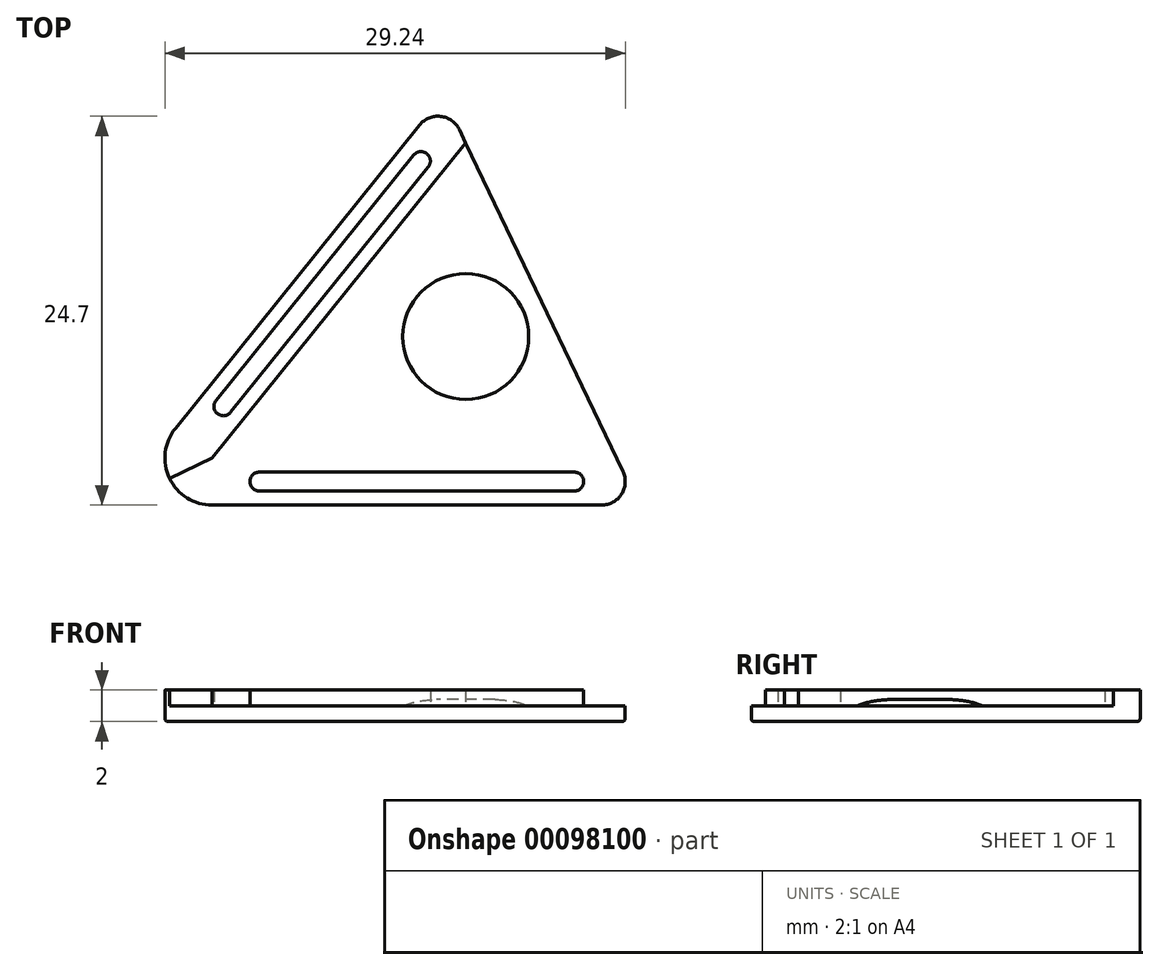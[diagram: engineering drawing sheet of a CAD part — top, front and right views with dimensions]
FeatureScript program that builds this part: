
annotation { "Feature Type Name" : "Feature", "Feature Type Description" : "" }
export const myFeature = defineFeature(function(context is Context, id is Id, definition is map)
    precondition{}
    {
        {
            var Q0;
            Q0=qCreatedBy(makeId("Top.planeOp"),FACE);
            var sketch = newSketch(context, id + "F0", { "sketchPlane" : qUnion([Q0])});
            skLineSegment(sketch, "E0", {"start": v(-16.1, 0) * mm, "end": v(0, 20) * mm});
            skLineSegment(sketch, "E1", {"start": v(0, 20) * mm, "end": v(9.57, 0) * mm});
            skLineSegment(sketch, "E2", {"start": v(9.57, 0) * mm, "end": v(-16.1, 0) * mm});
            skSolve(sketch);
        }
        {
            var Q0;
            Q0=makeQuery(id+"F0.imprint","IMPRINT",FACE,{"disambiguationData":[TD([[makeQuery(id+"F0.imprint","IMPRINT",EDGE,{"derivedFrom":sQuery(id+"F0.wireOp",EDGE,"E0")}),-1.0]])]});
            var sketch = newSketch(context, id + "F1", { "sketchPlane" : qUnion([Q0])});
            skLineSegment(sketch, "E3", {"start": v(-18.45, 1.88) * mm, "end": v(-1.44, 23) * mm});
            skLineSegment(sketch, "E4", {"start": v(-1.44, 23) * mm, "end": v(11, -3) * mm});
            skLineSegment(sketch, "E5", {"start": v(11, -3) * mm, "end": v(-16.1, -3) * mm});
            skPoint(sketch, "E6.visualSharp", {"position": v(-22.38, -3) * mm});
            skArc(sketch, "E6.filletArc", {"start": v(-18.45, 1.88) * mm, "mid": v(-18.82, -1.3) * mm, "end": v(-16.1, -3) * mm});
            skSolve(sketch);
        }
        {
            var Q0;
            Q0=makeQuery(id+"F0.imprint","IMPRINT",FACE,{"disambiguationData":[TD([[makeQuery(id+"F0.imprint","IMPRINT",EDGE,{"derivedFrom":sQuery(id+"F0.wireOp",EDGE,"E0")}),-1.0]])]});
            var Q1;
            {var subQ4=sQuery(id+"F1.wireOp",EDGE,"E3");Q1=makeQuery(id+"F1.imprint","IMPRINT",FACE,{"disambiguationData":[TD([[makeQuery(id+"F1.imprint","IMPRINT",EDGE,{"derivedFrom":subQ4}),-1.0]])]});}
            extrude(context, id + "F2", {"entities" : qUnion([Q0, Q1]), "depth" : 1 * mm});
        }
        {
            var Q0;
            Q0=makeQuery(id+"F2.opExtrude","CAP_FACE",FACE,{"disambiguationData":[OSD([sQuery(id+"F0.wireOp",EDGE,"E0"),sQuery(id+"F0.wireOp",EDGE,"E2"),sQuery(id+"F1.wireOp",EDGE,"E3"),sQuery(id+"F1.wireOp",EDGE,"E4"),sQuery(id+"F1.wireOp",EDGE,"E5")])],"isStart":false});
            var sketch = newSketch(context, id + "F3", { "sketchPlane" : qUnion([Q0])});
            skLineSegment(sketch, "E7", {"start": v(-16.1, 0) * mm, "end": v(0, 20) * mm});
            skLineSegment(sketch, "E8", {"start": v(0, 20) * mm, "end": v(-1.44, 23) * mm});
            skLineSegment(sketch, "E9", {"start": v(-1.44, 23) * mm, "end": v(-18.45, 1.88) * mm});
            skLineSegment(sketch, "E10", {"start": v(-16.1, 0) * mm, "end": v(-18.45, 1.88) * mm, "construction": true});
            skLineSegment(sketch, "E11", {"start": v(-13.1, -0.9) * mm, "end": v(6.9, -0.9) * mm});
            skLineSegment(sketch, "E12", {"start": v(6.9, -0.9) * mm, "end": v(6.9, -2.1) * mm, "construction": true});
            skLineSegment(sketch, "E13", {"start": v(6.9, -2.1) * mm, "end": v(-13.1, -2.1) * mm});
            skLineSegment(sketch, "E14", {"start": v(-13.1, -2.1) * mm, "end": v(-13.1, -0.9) * mm, "construction": true});
            skArc(sketch, "E15", {"start": v(6.9, -2.1) * mm, "mid": v(7.5, -1.5) * mm, "end": v(6.9, -0.9) * mm});
            skArc(sketch, "E16", {"start": v(-13.1, -0.9) * mm, "mid": v(-13.7, -1.5) * mm, "end": v(-13.1, -2.1) * mm});
            skLineSegment(sketch, "E17", {"start": v(-16.1, 0) * mm, "end": v(-16.1, -3) * mm, "construction": true});
            skLineSegment(sketch, "E18", {"start": v(-16.1, -1.5) * mm, "end": v(-4.74, -1.5) * mm, "construction": true});
            skLineSegment(sketch, "E19", {"start": v(-17.28, 0.94) * mm, "end": v(-10.44, 9.43) * mm, "construction": true});
            skLineSegment(sketch, "E20", {"start": v(-15.86, 3.65) * mm, "end": v(-3.32, 19.23) * mm});
            skLineSegment(sketch, "E21", {"start": v(-3.32, 19.23) * mm, "end": v(-2.38, 18.48) * mm, "construction": true});
            skLineSegment(sketch, "E22", {"start": v(-2.38, 18.48) * mm, "end": v(-14.93, 2.9) * mm});
            skLineSegment(sketch, "E23", {"start": v(-14.93, 2.9) * mm, "end": v(-15.86, 3.65) * mm, "construction": true});
            skPoint(sketch, "E24", {"position": v(-15.4, 3.28) * mm});
            skArc(sketch, "E25", {"start": v(-15.86, 3.65) * mm, "mid": v(-15.77, 2.81) * mm, "end": v(-14.93, 2.9) * mm});
            skArc(sketch, "E26", {"start": v(-2.38, 18.48) * mm, "mid": v(-2.47, 19.32) * mm, "end": v(-3.32, 19.23) * mm});
            skLineSegment(sketch, "E27", {"start": v(-16.1, 0) * mm, "end": v(-18.82, -1.3) * mm});
            skLineSegment(sketch, "E28", {"start": v(-18.45, 1.88) * mm, "end": v(-18.45, 1.88) * mm});
            skLineSegment(sketch, "E29", {"start": v(-18.82, -1.3) * mm, "end": v(-18.82, -1.3) * mm});
            skPoint(sketch, "E30.visualSharp", {"position": v(-19.63, 0.4) * mm});
            skArc(sketch, "E30.filletArc", {"start": v(-18.45, 1.88) * mm, "mid": v(-19.09, 0.35) * mm, "end": v(-18.82, -1.3) * mm});
            skSolve(sketch);
        }
        {
            var Q0;
            Q0=makeQuery(id+"F3.imprint","IMPRINT",FACE,{"disambiguationData":[TD([[makeQuery(id+"F3.imprint","IMPRINT",EDGE,{"derivedFrom":sQuery(id+"F3.wireOp",EDGE,"E7")}),1.0]])]});
            var Q1;
            Q1=makeQuery(id+"F3.imprint","IMPRINT",FACE,{"disambiguationData":[TD([[makeQuery(id+"F3.imprint","IMPRINT",EDGE,{"derivedFrom":sQuery(id+"F3.wireOp",EDGE,"E11")}),-1.0]])]});
            extrude(context, id + "F4", {"entities" : qUnion([Q0, Q1]), "depth" : 1 * mm});
        }
        {
            var Q0;
            Q0=makeQuery(id+"F4.opExtrude","SWEPT_EDGE",EDGE,{"disambiguationData":[OSD([sQuery(id+"F3.wireOp",EDGE,"E8"),sQuery(id+"F3.wireOp",EDGE,"E9")])]});
            var Q1;
            Q1=makeQuery(id+"F2.opExtrude","SWEPT_EDGE",EDGE,{"disambiguationData":[OSD([sQuery(id+"F1.wireOp",EDGE,"E3"),sQuery(id+"F1.wireOp",EDGE,"E4")])]});
            var Q2;
            Q2=makeQuery(id+"F2.opExtrude","SWEPT_EDGE",EDGE,{"disambiguationData":[OSD([sQuery(id+"F1.wireOp",EDGE,"E4"),sQuery(id+"F1.wireOp",EDGE,"E5")])]});
            fillet(context, id + "F5", {"entities" : qUnion([Q0, Q1, Q2]), "radius" : 1.5 * mm, "tangentPropagation" : true, "allowEdgeOverflow" : false});
        }
        {
            var Q0;
            Q0=makeQuery(id+"F2.opExtrude","CAP_FACE",FACE,{"disambiguationData":[OSD([sQuery(id+"F0.wireOp",EDGE,"E0"),sQuery(id+"F0.wireOp",EDGE,"E1"),sQuery(id+"F0.wireOp",EDGE,"E2")])],"isStart":false});
            var sketch = newSketch(context, id + "F6", { "sketchPlane" : qUnion([Q0])});
            skLineSegment(sketch, "E31", {"start": v(-16.1, 0) * mm, "end": v(4.79, 10) * mm, "construction": true});
            skCircle(sketch, "E32", {"center": v(0, 7.7) * mm, "radius": 4 * mm});
            skSolve(sketch);
        }
        {
            var Q0;
            Q0=makeQuery(id+"F6.imprint","IMPRINT",FACE,{"disambiguationData":[TD([[makeQuery(id+"F6.imprint","IMPRINT",EDGE,{"derivedFrom":sQuery(id+"F6.wireOp",EDGE,"E32")}),1.0]])]});
            extrude(context, id + "F7", {"entities" : qUnion([Q0]), "operationType" : NewBodyOperationType.ADD, "depth" : 0.4 * mm});
        }
        {
            var Q0;
            Q0=makeQuery(id+"F7.opExtrude","CAP_EDGE",EDGE,{"disambiguationData":[OSD([sQuery(id+"F6.wireOp",EDGE,"E32")])],"isStart":false});
            fillet(context, id + "F8", {"entities" : qUnion([Q0]), "radius" : 6 * mm, "tangentPropagation" : true, "allowEdgeOverflow" : false});
        }
        {
            var Q0;
            Q0=makeQuery(id+"F4.opExtrude","SWEPT_BODY",BODY,{"disambiguationData":[OSD([sQuery(id+"F3.wireOp",EDGE,"E7"),sQuery(id+"F3.wireOp",EDGE,"E8"),sQuery(id+"F3.wireOp",EDGE,"E9"),sQuery(id+"F3.wireOp",EDGE,"E20"),sQuery(id+"F3.wireOp",EDGE,"E22"),sQuery(id+"F3.wireOp",EDGE,"E25"),sQuery(id+"F3.wireOp",EDGE,"E26"),sQuery(id+"F3.wireOp",EDGE,"E27"),sQuery(id+"F3.wireOp",EDGE,"E30.filletArc")])]});
            var Q1;
            Q1=makeQuery(id+"F2.opExtrude","SWEPT_BODY",BODY,{"disambiguationData":[OSD([sQuery(id+"F0.wireOp",EDGE,"E0"),sQuery(id+"F0.wireOp",EDGE,"E1"),sQuery(id+"F0.wireOp",EDGE,"E2")])]});
            var Q2;
            Q2=makeQuery(id+"F2.opExtrude","SWEPT_BODY",BODY,{"disambiguationData":[OSD([sQuery(id+"F0.wireOp",EDGE,"E0"),sQuery(id+"F0.wireOp",EDGE,"E2"),sQuery(id+"F1.wireOp",EDGE,"E3"),sQuery(id+"F1.wireOp",EDGE,"E4"),sQuery(id+"F1.wireOp",EDGE,"E5"),sQuery(id+"F1.wireOp",EDGE,"E6.filletArc")])]});
            booleanBodies(context, id + "F9", {"operationType" : BooleanOperationType.UNION, "tools" : qUnion([Q0, Q1, Q2])});
        }
        {
            var Q0;
            {var subQ0=sQuery(id+"F1.wireOp",EDGE,"E4");Q0=makeQuery(id+"F9.opBoolean","MERGE",EDGE,{"derivedFrom":[makeQuery(id+"F2.opExtrude","CAP_EDGE",EDGE,{"disambiguationData":[OSD([sQuery(id+"F0.wireOp",EDGE,"E1")])],"isStart":true}),makeQuery(id+"F2.opExtrude","CAP_EDGE",EDGE,{"disambiguationData":[OSD([subQ0]),TDD([makeQuery(id+"F1.imprint","IMPRINT",EDGE,{"disambiguationData":[TD([[makeQuery(id+"F1.imprint","INTERSECT",VERTEX,{"derivedFrom":[makeQuery(id+"F0.imprint","IMPRINT",EDGE,{"derivedFrom":sQuery(id+"F0.wireOp",EDGE,"E0")}),subQ0]}),1.0]])],"derivedFrom":subQ0})])],"isStart":true}),makeQuery(id+"F2.opExtrude","CAP_EDGE",EDGE,{"disambiguationData":[OSD([subQ0]),TDD([makeQuery(id+"F1.imprint","IMPRINT",EDGE,{"disambiguationData":[TD([[makeQuery(id+"F1.imprint","INTERSECT",VERTEX,{"derivedFrom":[makeQuery(id+"F0.imprint","IMPRINT",EDGE,{"derivedFrom":sQuery(id+"F0.wireOp",EDGE,"E2")}),subQ0]}),-1.0]])],"derivedFrom":subQ0})])],"isStart":true})]});}
            var Q1;
            {var subQ0=sQuery(id+"F1.wireOp",EDGE,"E4");var subQ1=sQuery(id+"F1.wireOp",EDGE,"E3");Q1=makeQuery(id+"F5.opFillet","BLEND_EDGE",EDGE,{"blendedFrom":[makeQuery(id+"F2.opExtrude","SWEPT_EDGE",EDGE,{"disambiguationData":[OSD([subQ1,subQ0])]}),makeQuery(id+"F2.opExtrude","CAP_FACE",FACE,{"disambiguationData":[OSD([sQuery(id+"F0.wireOp",EDGE,"E0"),sQuery(id+"F0.wireOp",EDGE,"E2"),subQ1,subQ0,sQuery(id+"F1.wireOp",EDGE,"E5"),sQuery(id+"F1.wireOp",EDGE,"E6.filletArc")])],"isStart":true})],"blendedInto":[makeQuery(id+"F2.opExtrude","CAP_FACE",FACE,{"disambiguationData":[OSD([sQuery(id+"F0.wireOp",EDGE,"E0"),sQuery(id+"F0.wireOp",EDGE,"E2"),subQ1,subQ0,sQuery(id+"F1.wireOp",EDGE,"E5"),sQuery(id+"F1.wireOp",EDGE,"E6.filletArc")])],"isStart":true})]});}
            var Q2;
            Q2=makeQuery(id+"F2.opExtrude","CAP_EDGE",EDGE,{"disambiguationData":[OSD([sQuery(id+"F1.wireOp",EDGE,"E3")])],"isStart":true});
            var Q3;
            Q3=makeQuery(id+"F2.opExtrude","CAP_EDGE",EDGE,{"disambiguationData":[OSD([sQuery(id+"F1.wireOp",EDGE,"E6.filletArc")])],"isStart":true});
            var Q4;
            Q4=makeQuery(id+"F2.opExtrude","CAP_EDGE",EDGE,{"disambiguationData":[OSD([sQuery(id+"F1.wireOp",EDGE,"E5")])],"isStart":true});
            var Q5;
            {var subQ0=sQuery(id+"F1.wireOp",EDGE,"E5");var subQ1=sQuery(id+"F1.wireOp",EDGE,"E4");Q5=makeQuery(id+"F5.opFillet","BLEND_EDGE",EDGE,{"blendedFrom":[makeQuery(id+"F2.opExtrude","SWEPT_EDGE",EDGE,{"disambiguationData":[OSD([subQ1,subQ0])]}),makeQuery(id+"F2.opExtrude","CAP_FACE",FACE,{"disambiguationData":[OSD([sQuery(id+"F0.wireOp",EDGE,"E0"),sQuery(id+"F0.wireOp",EDGE,"E2"),sQuery(id+"F1.wireOp",EDGE,"E3"),subQ1,subQ0,sQuery(id+"F1.wireOp",EDGE,"E6.filletArc")])],"isStart":true})],"blendedInto":[makeQuery(id+"F2.opExtrude","CAP_FACE",FACE,{"disambiguationData":[OSD([sQuery(id+"F0.wireOp",EDGE,"E0"),sQuery(id+"F0.wireOp",EDGE,"E2"),sQuery(id+"F1.wireOp",EDGE,"E3"),subQ1,subQ0,sQuery(id+"F1.wireOp",EDGE,"E6.filletArc")])],"isStart":true})]});}
            fillet(context, id + "F10", {"entities" : qUnion([Q0, Q1, Q2, Q3, Q4, Q5]), "radius" : 0.2 * mm, "tangentPropagation" : true, "allowEdgeOverflow" : false});
        }
    });
